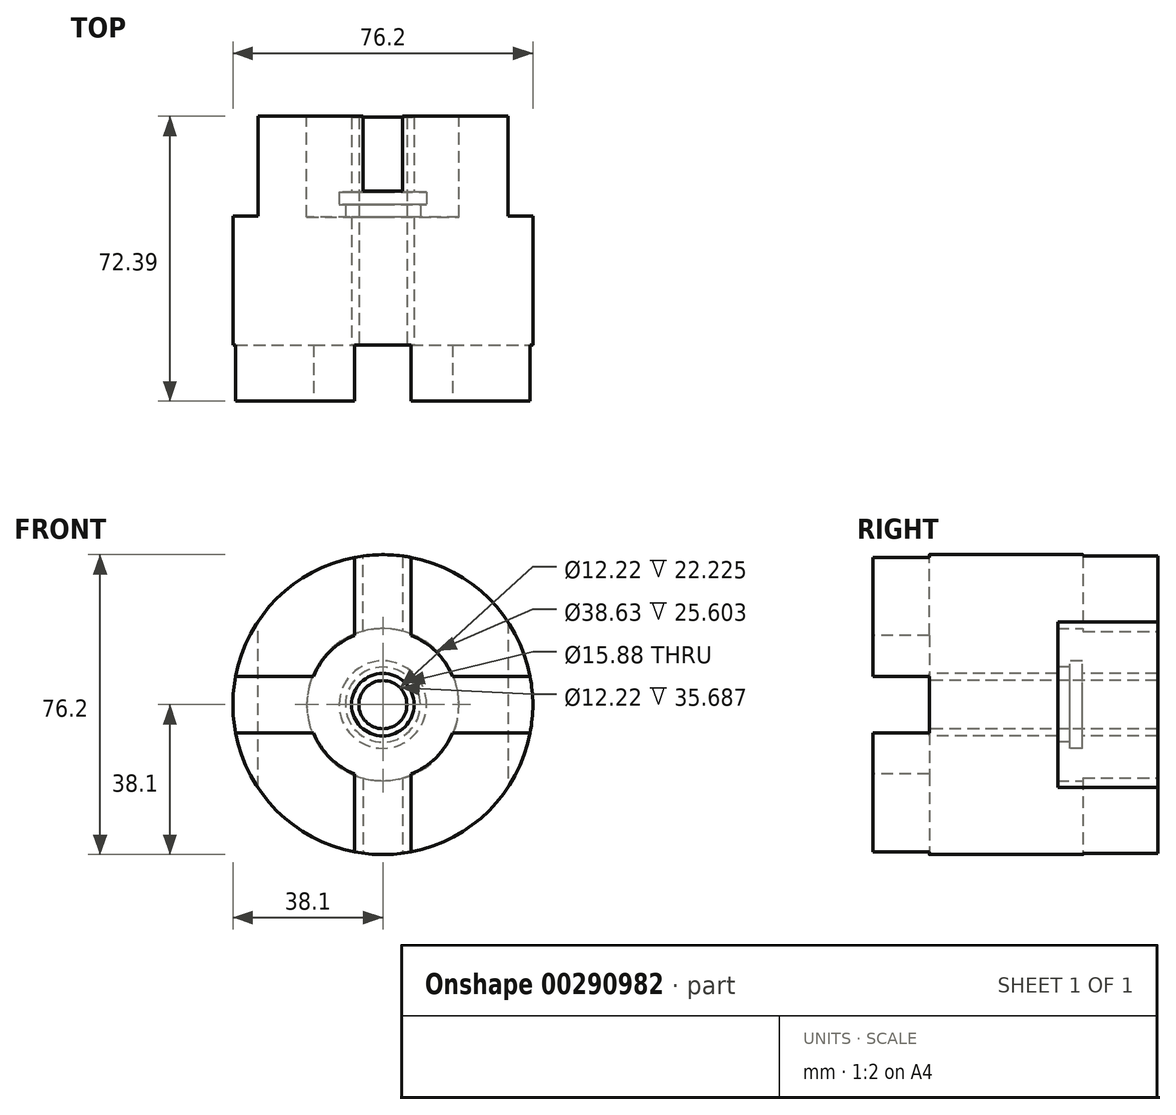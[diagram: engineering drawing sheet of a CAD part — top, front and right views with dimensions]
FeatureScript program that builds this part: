
annotation { "Feature Type Name" : "Feature", "Feature Type Description" : "" }
export const myFeature = defineFeature(function(context is Context, id is Id, definition is map)
    precondition{}
    {
        {
            var Q0;
            Q0=qCreatedBy(makeId("Right.planeOp"),FACE);
            var sketch = newSketch(context, id + "F0", { "sketchPlane" : qUnion([Q0])});
            skLineSegment(sketch, "E0", {"start": v(0, 19.05) * mm, "end": v(0, 38.1) * mm});
            skLineSegment(sketch, "E1", {"start": v(0, 38.1) * mm, "end": v(72.4, 38.1) * mm});
            skLineSegment(sketch, "E2", {"start": v(72.4, 38.1) * mm, "end": v(72.4, 19.32) * mm});
            skLineSegment(sketch, "E3", {"start": v(72.4, 19.32) * mm, "end": v(46.79, 19.32) * mm});
            skLineSegment(sketch, "E4", {"start": v(46.79, 19.32) * mm, "end": v(46.79, 0) * mm});
            skLineSegment(sketch, "E5", {"start": v(46.79, 0) * mm, "end": v(14.27, 0) * mm});
            skLineSegment(sketch, "E6", {"start": v(14.27, 0) * mm, "end": v(14.27, 19.05) * mm});
            skLineSegment(sketch, "E7", {"start": v(14.27, 19.05) * mm, "end": v(0, 19.05) * mm});
            skSolve(sketch);
        }
        {
            var Q0;
            Q0=makeQuery(id+"F0.imprint","IMPRINT",FACE,{"disambiguationData":[TD([[makeQuery(id+"F0.imprint","IMPRINT",EDGE,{"derivedFrom":sQuery(id+"F0.wireOp",EDGE,"E0")}),-1.0]])]});
            var Q1;
            Q1=sQuery(id+"F0.wireOp",EDGE,"E5");
            revolve(context, id + "F1", {"entities" : qUnion([Q0]), "axis" : qUnion([Q1]), "revolveType" : RevolveType.FULL});
        }
        {
            var Q0;
            Q0=makeQuery(id+"F1.opRevolve","SWEPT_FACE",FACE,{"disambiguationData":[OSD([sQuery(id+"F0.wireOp",EDGE,"E6")])]});
            var sketch = newSketch(context, id + "F2", { "sketchPlane" : qUnion([Q0])});
            skPoint(sketch, "E8", {"position": v(0, 0) * mm});
            skSolve(sketch);
        }
        {
            var Q0;
            Q0=sQuery(id+"F2.wireOp",VERTEX,"E8");
            var Q1;
            Q1=makeQuery(id+"F1.opRevolve","SWEPT_BODY",BODY,{"disambiguationData":[OSD([sQuery(id+"F0.wireOp",EDGE,"E0"),sQuery(id+"F0.wireOp",EDGE,"E1"),sQuery(id+"F0.wireOp",EDGE,"E2"),sQuery(id+"F0.wireOp",EDGE,"E3"),sQuery(id+"F0.wireOp",EDGE,"E4"),sQuery(id+"F0.wireOp",EDGE,"E5"),sQuery(id+"F0.wireOp",EDGE,"E6"),sQuery(id+"F0.wireOp",EDGE,"E7")])]});
            hole(context, id + "F3", {"style" : HoleStyle.SIMPLE, "endStyle" : HoleEndStyle.THROUGH, "holeDiameter" : 15.88 * mm, "tappedDepth" : 12.7 * mm, "tapClearance" : 5, "startFromSketch" : true, "locations" : qUnion([Q0]), "scope" : qUnion([Q1])});
        }
        {
            var Q0;
            Q0=makeQuery(id+"F1.opRevolve","SWEPT_FACE",FACE,{"disambiguationData":[OSD([sQuery(id+"F0.wireOp",EDGE,"E0")])]});
            var sketch = newSketch(context, id + "F4", { "sketchPlane" : qUnion([Q0])});
            skArc(sketch, "E9.0", {"start": v(-17.65, 7.18) * mm, "mid": v(-19.05, 0) * mm, "end": v(-17.65, -7.18) * mm});
            skArc(sketch, "E10.0", {"start": v(-37.42, 7.18) * mm, "mid": v(-38.1, 0) * mm, "end": v(-37.42, -7.18) * mm});
            skLineSegment(sketch, "E11", {"start": v(-7.18, 17.65) * mm, "end": v(-7.18, 37.42) * mm});
            skLineSegment(sketch, "E12", {"start": v(7.18, 17.65) * mm, "end": v(7.18, 37.42) * mm});
            skLineSegment(sketch, "E13", {"start": v(-7.18, -17.65) * mm, "end": v(-7.18, -37.42) * mm});
            skLineSegment(sketch, "E14", {"start": v(7.18, -17.65) * mm, "end": v(7.18, -37.42) * mm});
            skLineSegment(sketch, "E15", {"start": v(-17.65, 7.18) * mm, "end": v(-37.42, 7.18) * mm});
            skLineSegment(sketch, "E16", {"start": v(-37.42, -7.18) * mm, "end": v(-17.65, -7.18) * mm});
            skLineSegment(sketch, "E17", {"start": v(17.65, 7.18) * mm, "end": v(37.42, 7.18) * mm});
            skLineSegment(sketch, "E18", {"start": v(17.65, -7.18) * mm, "end": v(37.42, -7.18) * mm});
            skArc(sketch, "E19.trimOffspring", {"start": v(7.18, 17.65) * mm, "mid": v(0, 19.05) * mm, "end": v(-7.18, 17.65) * mm});
            skArc(sketch, "E20.trimOffspring", {"start": v(7.18, 37.42) * mm, "mid": v(0, 38.1) * mm, "end": v(-7.18, 37.42) * mm});
            skArc(sketch, "E21.trimOffspring", {"start": v(37.42, -7.18) * mm, "mid": v(38.1, 0) * mm, "end": v(37.42, 7.18) * mm});
            skArc(sketch, "E22.trimOffspring", {"start": v(17.65, -7.18) * mm, "mid": v(19.05, 0) * mm, "end": v(17.65, 7.18) * mm});
            skArc(sketch, "E23.trimOffspring", {"start": v(-7.18, -17.65) * mm, "mid": v(0, -19.05) * mm, "end": v(7.18, -17.65) * mm});
            skArc(sketch, "E24.trimOffspring", {"start": v(-7.18, -37.42) * mm, "mid": v(0, -38.1) * mm, "end": v(7.18, -37.42) * mm});
            skSolve(sketch);
        }
        {
            var Q0;
            Q0=makeQuery(id+"F4.imprint","IMPRINT",FACE,{"disambiguationData":[TD([[makeQuery(id+"F4.imprint","IMPRINT",EDGE,{"derivedFrom":sQuery(id+"F4.wireOp",EDGE,"E11")}),-1.0]])]});
            var Q1;
            Q1=makeQuery(id+"F4.imprint","IMPRINT",FACE,{"disambiguationData":[TD([[makeQuery(id+"F4.imprint","IMPRINT",EDGE,{"derivedFrom":sQuery(id+"F4.wireOp",EDGE,"E9.0")}),1.0]])]});
            var Q2;
            Q2=makeQuery(id+"F4.imprint","IMPRINT",FACE,{"disambiguationData":[TD([[makeQuery(id+"F4.imprint","IMPRINT",EDGE,{"derivedFrom":sQuery(id+"F4.wireOp",EDGE,"E17")}),-1.0]])]});
            var Q3;
            Q3=makeQuery(id+"F4.imprint","IMPRINT",FACE,{"disambiguationData":[TD([[makeQuery(id+"F4.imprint","IMPRINT",EDGE,{"derivedFrom":sQuery(id+"F4.wireOp",EDGE,"E13")}),1.0]])]});
            var Q4;
            Q4=makeQuery(id+"F1.opRevolve","SWEPT_FACE",FACE,{"disambiguationData":[OSD([sQuery(id+"F0.wireOp",EDGE,"E6")])]});
            extrude(context, id + "F5", {"entities" : qUnion([Q0, Q1, Q2, Q3]), "operationType" : NewBodyOperationType.REMOVE, "endBound" : BoundingType.UP_TO_SURFACE, "oppositeDirection" : true, "endBoundEntityFace" : qUnion([Q4]), "depth" : 25.4 * mm});
        }
        {
            var Q0;
            Q0=makeQuery(id+"F1.opRevolve","SWEPT_FACE",FACE,{"disambiguationData":[OSD([sQuery(id+"F0.wireOp",EDGE,"E2")])]});
            var sketch = newSketch(context, id + "F6", { "sketchPlane" : qUnion([Q0])});
            skArc(sketch, "E25.0", {"start": v(-31.75, 21.06) * mm, "mid": v(-38.1, 0) * mm, "end": v(-31.75, -21.06) * mm});
            skLineSegment(sketch, "E26", {"start": v(-31.75, 21.06) * mm, "end": v(-31.75, -21.06) * mm});
            skLineSegment(sketch, "E27", {"start": v(31.75, -21.06) * mm, "end": v(31.75, 21.06) * mm});
            skArc(sketch, "E28.trimOffspring", {"start": v(31.75, -21.06) * mm, "mid": v(38.1, 0) * mm, "end": v(31.75, 21.06) * mm});
            skSolve(sketch);
        }
        {
            var Q0;
            Q0=makeQuery(id+"F6.imprint","IMPRINT",FACE,{"disambiguationData":[TD([[makeQuery(id+"F6.imprint","IMPRINT",EDGE,{"derivedFrom":sQuery(id+"F6.wireOp",EDGE,"E25.0")}),1.0]])]});
            var Q1;
            Q1=makeQuery(id+"F6.imprint","IMPRINT",FACE,{"disambiguationData":[TD([[makeQuery(id+"F6.imprint","IMPRINT",EDGE,{"derivedFrom":sQuery(id+"F6.wireOp",EDGE,"E27")}),-1.0]])]});
            extrude(context, id + "F7", {"entities" : qUnion([Q0, Q1]), "operationType" : NewBodyOperationType.REMOVE, "oppositeDirection" : true, "depth" : 25.4 * mm});
        }
        {
            var Q0;
            Q0=makeQuery(id+"F1.opRevolve","SWEPT_FACE",FACE,{"disambiguationData":[OSD([sQuery(id+"F0.wireOp",EDGE,"E2")])]});
            var sketch = newSketch(context, id + "F8", { "sketchPlane" : qUnion([Q0])});
            skLineSegment(sketch, "E29", {"start": v(-5.02, 37.77) * mm, "end": v(-5.02, 18.65) * mm});
            skLineSegment(sketch, "E30", {"start": v(5.02, 18.65) * mm, "end": v(5.02, 37.77) * mm});
            skLineSegment(sketch, "E31", {"start": v(-5.02, -18.65) * mm, "end": v(-5.02, -37.77) * mm});
            skLineSegment(sketch, "E32", {"start": v(5.02, -18.65) * mm, "end": v(5.02, -37.77) * mm});
            skSolve(sketch);
        }
        {
            var Q0;
            {var subQ0=sQuery(id+"F8.wireOp",EDGE,"E29");Q0=makeQuery(id+"F8.imprint","IMPRINT",FACE,{"disambiguationData":[TD([[makeQuery(id+"F8.imprint","IMPRINT",EDGE,{"derivedFrom":subQ0}),1.0]])]});}
            var Q1;
            {var subQ0=sQuery(id+"F8.wireOp",EDGE,"E31");Q1=makeQuery(id+"F8.imprint","IMPRINT",FACE,{"disambiguationData":[TD([[makeQuery(id+"F8.imprint","IMPRINT",EDGE,{"derivedFrom":subQ0}),1.0]])]});}
            extrude(context, id + "F9", {"entities" : qUnion([Q0, Q1]), "operationType" : NewBodyOperationType.REMOVE, "oppositeDirection" : true, "depth" : 19.05 * mm});
        }
        {
            var Q0;
            Q0=qCreatedBy(makeId("Right.planeOp"),FACE);
            var sketch = newSketch(context, id + "F10", { "sketchPlane" : qUnion([Q0])});
            skLineSegment(sketch, "E33", {"start": v(14.27, 7.94) * mm, "end": v(46.79, 7.94) * mm});
            skLineSegment(sketch, "E34", {"start": v(46.79, 7.94) * mm, "end": v(46.79, 9.53) * mm});
            skLineSegment(sketch, "E35", {"start": v(46.79, 9.53) * mm, "end": v(49.96, 9.53) * mm});
            skLineSegment(sketch, "E36", {"start": v(49.96, 9.53) * mm, "end": v(49.96, 6.1) * mm});
            skLineSegment(sketch, "E37", {"start": v(49.96, 6.1) * mm, "end": v(14.27, 6.1) * mm});
            skLineSegment(sketch, "E38", {"start": v(14.27, 6.1) * mm, "end": v(14.27, 7.94) * mm});
            skLineSegment(sketch, "E39", {"start": v(0, 0) * mm, "end": v(51.1, 0) * mm});
            skSolve(sketch);
        }
        {
            var Q0;
            Q0=makeQuery(id+"F10.imprint","IMPRINT",FACE,{"disambiguationData":[TD([[makeQuery(id+"F10.imprint","IMPRINT",EDGE,{"derivedFrom":sQuery(id+"F10.wireOp",EDGE,"E33")}),-1.0]])]});
            var Q1;
            Q1=sQuery(id+"F10.wireOp",EDGE,"E39");
            revolve(context, id + "F11", {"entities" : qUnion([Q0]), "axis" : qUnion([Q1]), "revolveType" : RevolveType.FULL});
        }
        {
            var Q0;
            Q0=qCreatedBy(makeId("Right.planeOp"),FACE);
            var sketch = newSketch(context, id + "F12", { "sketchPlane" : qUnion([Q0])});
            skLineSegment(sketch, "E40", {"start": v(49.96, 11.11) * mm, "end": v(49.96, 6.1) * mm});
            skLineSegment(sketch, "E41", {"start": v(49.96, 6.1) * mm, "end": v(72.19, 6.1) * mm});
            skLineSegment(sketch, "E42", {"start": v(72.19, 6.1) * mm, "end": v(72.19, 7.94) * mm});
            skLineSegment(sketch, "E43", {"start": v(72.19, 7.94) * mm, "end": v(53.14, 7.94) * mm});
            skLineSegment(sketch, "E44", {"start": v(53.14, 7.94) * mm, "end": v(53.14, 11.11) * mm});
            skLineSegment(sketch, "E45", {"start": v(53.14, 11.11) * mm, "end": v(49.96, 11.11) * mm});
            skLineSegment(sketch, "E46", {"start": v(49.96, 0) * mm, "end": v(80.74, 0) * mm});
            skSolve(sketch);
        }
        {
            var Q0;
            Q0=makeQuery(id+"F12.imprint","IMPRINT",FACE,{"disambiguationData":[TD([[makeQuery(id+"F12.imprint","IMPRINT",EDGE,{"derivedFrom":sQuery(id+"F12.wireOp",EDGE,"E40")}),1.0]])]});
            var Q1;
            Q1=sQuery(id+"F12.wireOp",EDGE,"E46");
            revolve(context, id + "F13", {"entities" : qUnion([Q0]), "axis" : qUnion([Q1]), "revolveType" : RevolveType.FULL});
        }
    });
